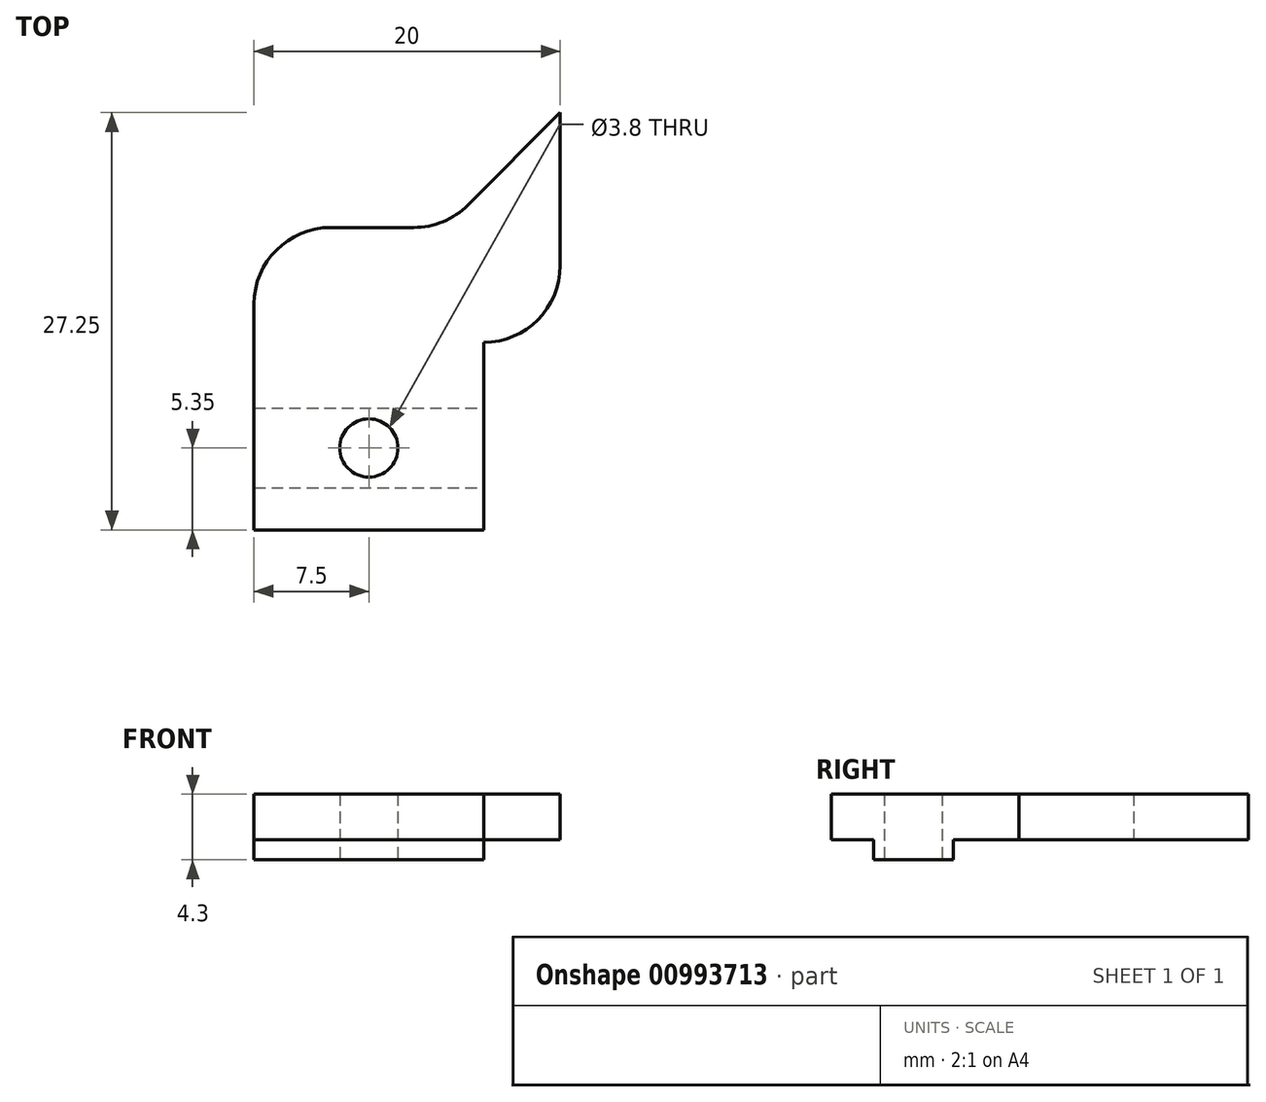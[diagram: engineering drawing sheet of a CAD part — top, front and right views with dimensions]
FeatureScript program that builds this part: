
annotation { "Feature Type Name" : "Feature", "Feature Type Description" : "" }
export const myFeature = defineFeature(function(context is Context, id is Id, definition is map)
    precondition{}
    {
        {
            var Q0;
            Q0=qCreatedBy(makeId("Top.planeOp"),FACE);
            var sketch = newSketch(context, id + "F0", { "sketchPlane" : qUnion([Q0])});
            skLineSegment(sketch, "E0", {"start": v(-7.5, 7.45) * mm, "end": v(-7.5, 10.2) * mm});
            skLineSegment(sketch, "E1", {"start": v(-7.5, 10.2) * mm, "end": v(-7.5, 15.4) * mm});
            skLineSegment(sketch, "E2", {"start": v(-7.5, 15.4) * mm, "end": v(-7.5, 19.7) * mm});
            skLineSegment(sketch, "E3", {"start": v(7.5, 15.4) * mm, "end": v(7.5, 10.2) * mm});
            skLineSegment(sketch, "E4", {"start": v(7.5, 10.2) * mm, "end": v(7.5, 7.45) * mm});
            skLineSegment(sketch, "E5", {"start": v(7.5, 7.45) * mm, "end": v(-7.5, 7.45) * mm});
            skLineSegment(sketch, "E6", {"start": v(-7.5, 10.2) * mm, "end": v(7.5, 10.2) * mm});
            skLineSegment(sketch, "E7", {"start": v(-7.5, 15.4) * mm, "end": v(7.5, 15.4) * mm});
            skLineSegment(sketch, "E8", {"start": v(7.5, 15.4) * mm, "end": v(7.5, 19.7) * mm});
            skLineSegment(sketch, "E9", {"start": v(7.5, 19.7) * mm, "end": v(12.5, 19.7) * mm});
            skLineSegment(sketch, "E10", {"start": v(12.5, 19.7) * mm, "end": v(12.5, 34.7) * mm});
            skCircle(sketch, "E11", {"center": v(0, 12.8) * mm, "radius": 1.9 * mm});
            skLineSegment(sketch, "E12", {"start": v(-7.5, 19.7) * mm, "end": v(7.5, 19.7) * mm});
            skLineSegment(sketch, "E13", {"start": v(12.5, 34.7) * mm, "end": v(5, 27.2) * mm});
            skLineSegment(sketch, "E14", {"start": v(5, 27.2) * mm, "end": v(-7.5, 27.2) * mm});
            skLineSegment(sketch, "E15", {"start": v(-7.5, 27.2) * mm, "end": v(-7.5, 19.7) * mm});
            skSolve(sketch);
        }
        {
            var Q0;
            Q0 = qSketchRegion(id + "F0", true);
            extrude(context, id + "F1", {"entities" : qUnion([Q0]), "depth" : 3 * mm, "offsetDistance" : 25 * mm});
        }
        {
            var Q0;
            Q0=makeQuery(id+"F0.imprint","IMPRINT",FACE,{"disambiguationData":[TD([[makeQuery(id+"F0.imprint","IMPRINT",EDGE,{"derivedFrom":sQuery(id+"F0.wireOp",EDGE,"E1")}),-1.0]])]});
            var Q1;
            Q1=makeQuery(id+"F0.imprint","IMPRINT",FACE,{"disambiguationData":[TD([[makeQuery(id+"F0.imprint","IMPRINT",EDGE,{"derivedFrom":sQuery(id+"F0.wireOp",EDGE,"XM0VbCyx-99xj-YghP-UF3m-zCLUwLXzifZy")}),-1.0]])]});
            extrude(context, id + "F2", {"entities" : qUnion([Q0, Q1]), "operationType" : NewBodyOperationType.ADD, "oppositeDirection" : true, "depth" : 1.3 * mm, "offsetDistance" : 25 * mm});
        }
        {
            var Q0;
            Q0=makeQuery(id+"F1.opExtrude","SWEPT_EDGE",EDGE,{"disambiguationData":[OSD([sQuery(id+"F0.wireOp",EDGE,"E9"),sQuery(id+"F0.wireOp",EDGE,"E10")])]});
            var Q1;
            Q1=makeQuery(id+"F1.opExtrude","SWEPT_EDGE",EDGE,{"disambiguationData":[OSD([sQuery(id+"F0.wireOp",EDGE,"E14"),sQuery(id+"F0.wireOp",EDGE,"E15")])]});
            var Q2;
            Q2=makeQuery(id+"F1.opExtrude","SWEPT_EDGE",EDGE,{"disambiguationData":[OSD([sQuery(id+"F0.wireOp",EDGE,"E13"),sQuery(id+"F0.wireOp",EDGE,"E14")])]});
            fillet(context, id + "F3", {"entities" : qUnion([Q0, Q1, Q2]), "radius" : 5 * mm, "tangentPropagation" : true, "allowEdgeOverflow" : false});
        }
    });
